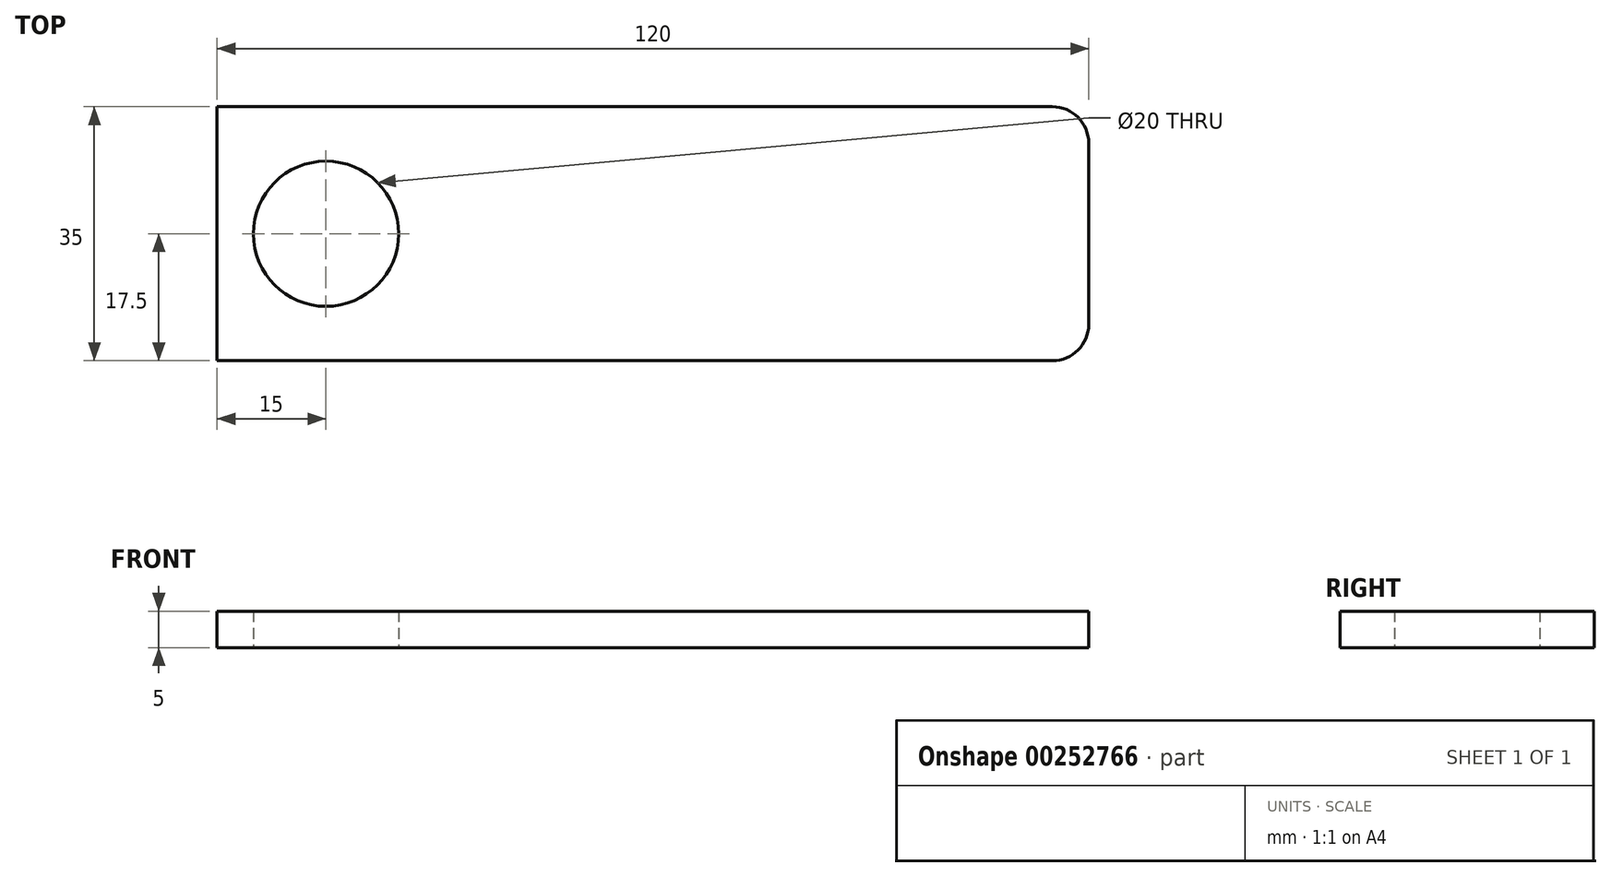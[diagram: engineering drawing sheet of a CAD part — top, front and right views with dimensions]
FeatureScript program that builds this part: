
annotation { "Feature Type Name" : "Feature", "Feature Type Description" : "" }
export const myFeature = defineFeature(function(context is Context, id is Id, definition is map)
    precondition{}
    {
        {
            var Q0;
            Q0=qCreatedBy(makeId("Top.planeOp"),FACE);
            var sketch = newSketch(context, id + "F0", { "sketchPlane" : qUnion([Q0])});
            skLineSegment(sketch, "E0.bottom", {"start": v(-60, 17.5) * mm, "end": v(60, 17.5) * mm});
            skLineSegment(sketch, "E0.top", {"start": v(-60, -17.5) * mm, "end": v(60, -17.5) * mm});
            skLineSegment(sketch, "E0.left", {"start": v(-60, 17.5) * mm, "end": v(-60, -17.5) * mm});
            skLineSegment(sketch, "E0.right", {"start": v(60, 17.5) * mm, "end": v(60, -17.5) * mm});
            skPoint(sketch, "E0.middle", {"position": v(0, 0) * mm});
            skCircle(sketch, "E1", {"center": v(-45, 0) * mm, "radius": 10 * mm});
            skPoint(sketch, "E1.centerSnap0", {"position": v(-60, 0) * mm});
            skSolve(sketch);
        }
        {
            var Q0;
            Q0=makeQuery(id+"F0.imprint","IMPRINT",FACE,{"disambiguationData":[TD([[makeQuery(id+"F0.imprint","IMPRINT",EDGE,{"derivedFrom":sQuery(id+"F0.wireOp",EDGE,"E0.bottom")}),-1.0]])]});
            extrude(context, id + "F1", {"entities" : qUnion([Q0]), "depth" : 5 * mm});
        }
        {
            var Q0;
            Q0=makeQuery(id+"F1.opExtrude","SWEPT_EDGE",EDGE,{"disambiguationData":[OSD([sQuery(id+"F0.wireOp",EDGE,"E0.top"),sQuery(id+"F0.wireOp",EDGE,"E0.right")])]});
            fillet(context, id + "F2", {"entities" : qUnion([Q0]), "radius" : 5 * mm, "tangentPropagation" : true, "allowEdgeOverflow" : false});
        }
        {
            var Q0;
            Q0=makeQuery(id+"F1.opExtrude","SWEPT_EDGE",EDGE,{"disambiguationData":[OSD([sQuery(id+"F0.wireOp",EDGE,"E0.bottom"),sQuery(id+"F0.wireOp",EDGE,"E0.right")])]});
            fillet(context, id + "F3", {"entities" : qUnion([Q0]), "radius" : 5 * mm, "tangentPropagation" : true, "allowEdgeOverflow" : false});
        }
    });
